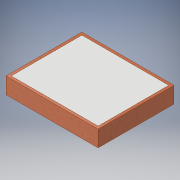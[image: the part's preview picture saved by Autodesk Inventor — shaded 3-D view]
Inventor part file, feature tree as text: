
AUTODESK INVENTOR PART (.ipt)
format: ipt  version: 2017 (Build 210142000, 142)  size: 128,000 bytes
history: native  units: in
note: dims shown in document units (in); Inventor stores cm internally (conversion verified against a paired STEP export)
features: extrude x3, sketch x3
ambient origin geometry x8: Origin, YZ Plane, XZ Plane, XY Plane, X Axis, Y Axis, Z Axis, Center Point
bodies: Solid1 (feature_tree)
feature tree (6):
  extrude  "Extrusion1"  Depth=5.5118in
  extrude  "Extrusion2"  Depth=0.1875in
  extrude  "Extrusion3"  Depth=0.1875in
  sketch  "Sketch1"  dims[d0=6.6929in d1=5.5118in]
  sketch  "Sketch2"  dims[d2=0.1875in d3=0.1875in]
  sketch  "Sketch3"  dims[d4=0.1875in d5=0.1875in d6=0.1875in d7=1.1811in d8=0.0in d9=0.5in d10=0.0in d11=0.001in d12=0.0in]
